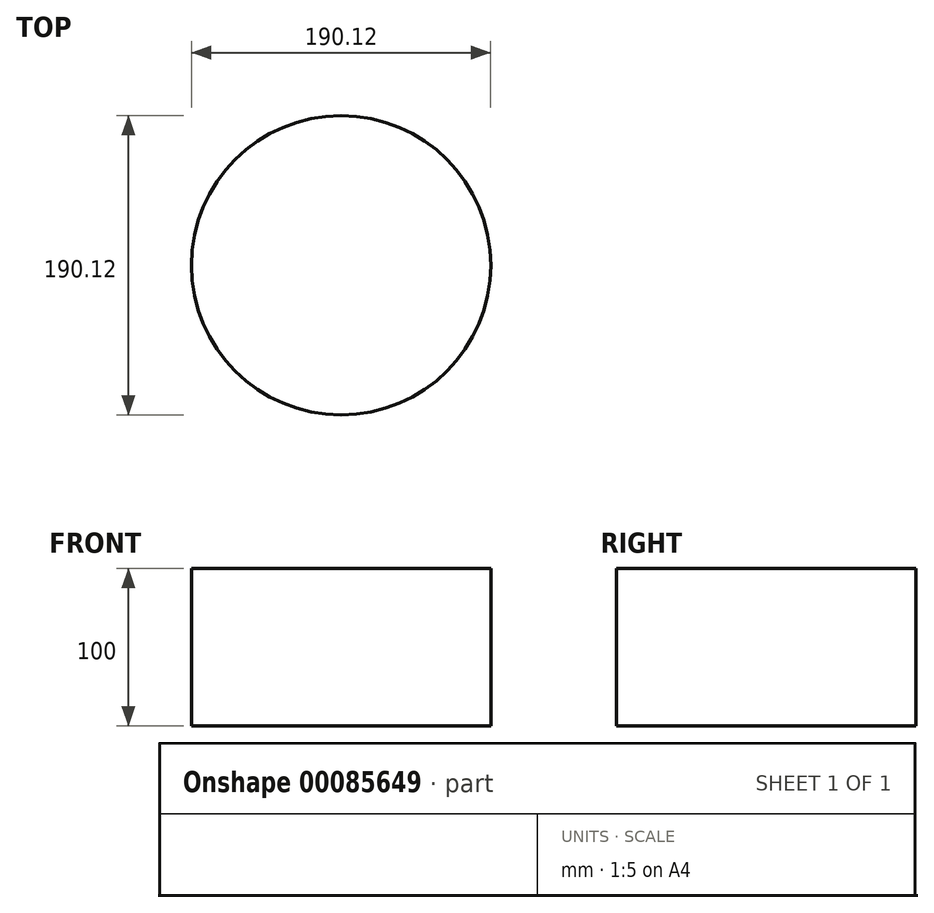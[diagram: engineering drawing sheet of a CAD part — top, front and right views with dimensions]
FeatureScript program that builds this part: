
annotation { "Feature Type Name" : "Feature", "Feature Type Description" : "" }
export const myFeature = defineFeature(function(context is Context, id is Id, definition is map)
    precondition{}
    {
        {
            var Q0;
            Q0=qCreatedBy(makeId("Top.planeOp"),FACE);
            var sketch = newSketch(context, id + "F0", { "sketchPlane" : qUnion([Q0])});
            skCircle(sketch, "E0", {"center": v(0, 0) * mm, "radius": 95.06 * mm});
            skSolve(sketch);
        }
        {
            var Q0;
            Q0=makeQuery(id+"F0.imprint","IMPRINT",FACE,{"disambiguationData":[TD([[makeQuery(id+"F0.imprint","IMPRINT",EDGE,{"derivedFrom":sQuery(id+"F0.wireOp",EDGE,"E0")}),1.0]])]});
            var Q1;
            Q1=sQuery(id+"F0.wireOp",EDGE,"E0");
            extrude(context, id + "F1", {"entities" : qUnion([Q0]), "bodyType" : ToolBodyType.SURFACE, "surfaceEntities" : qUnion([Q1]), "depth" : 100 * mm});
        }
    });
